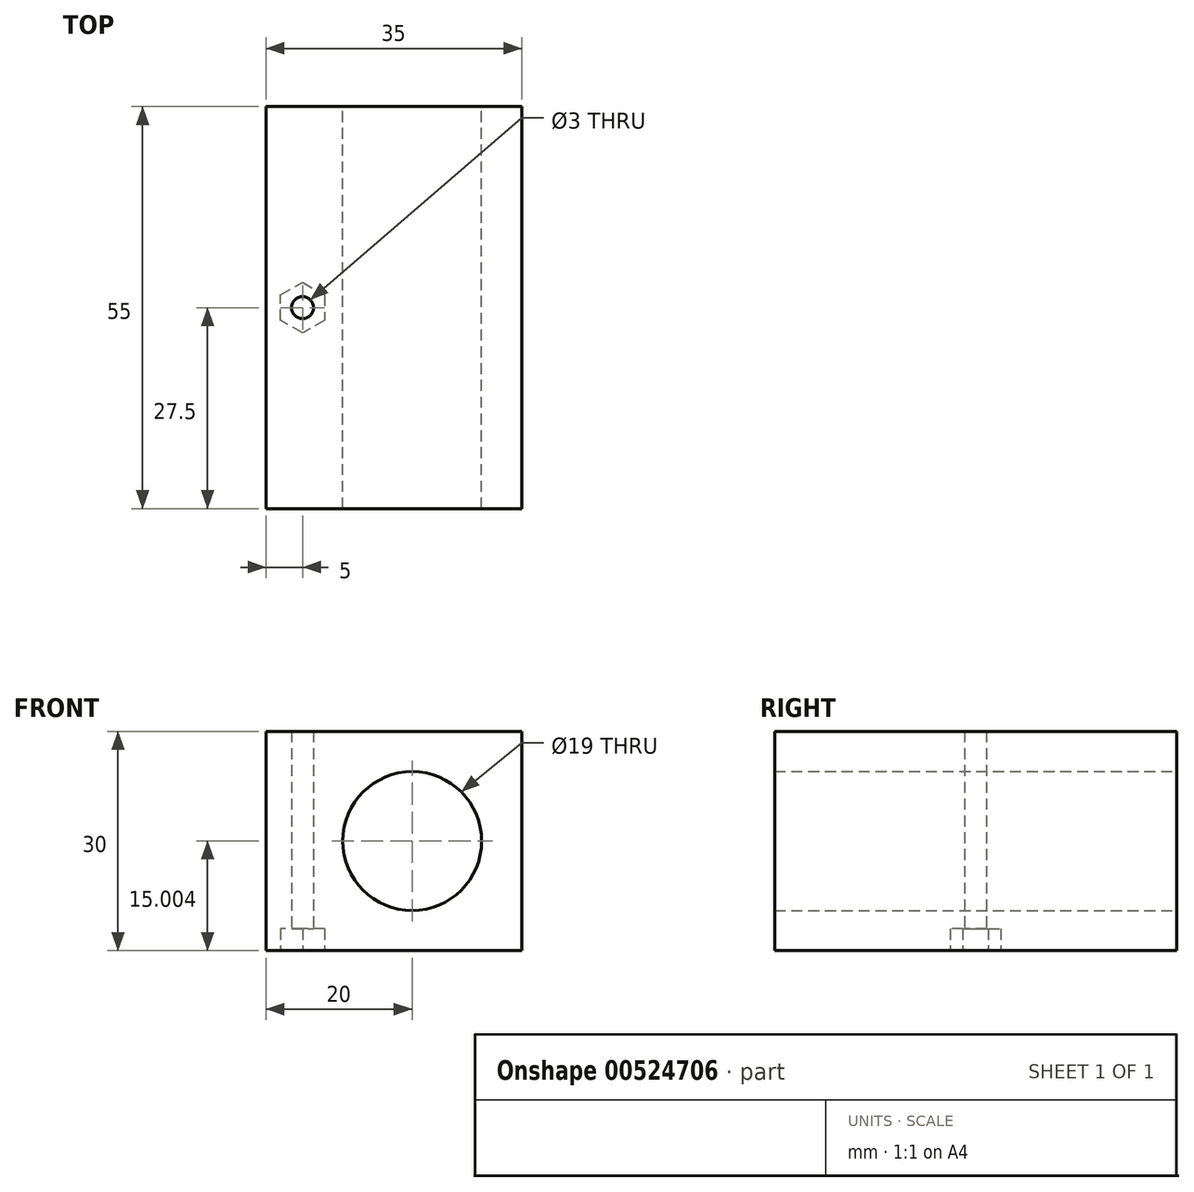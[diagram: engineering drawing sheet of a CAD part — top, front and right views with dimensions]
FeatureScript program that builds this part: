
annotation { "Feature Type Name" : "Feature", "Feature Type Description" : "" }
export const myFeature = defineFeature(function(context is Context, id is Id, definition is map)
    precondition{}
    {
        {
            var Q0;
            Q0=qCreatedBy(makeId("Front.planeOp"),FACE);
            var sketch = newSketch(context, id + "F0", { "sketchPlane" : qUnion([Q0])});
            skLineSegment(sketch, "E0.bottom", {"start": v(-25, 4.92) * mm, "end": v(10, 4.92) * mm});
            skLineSegment(sketch, "E0.top", {"start": v(-25, -25.08) * mm, "end": v(10, -25.08) * mm});
            skLineSegment(sketch, "E0.left", {"start": v(-25, 4.92) * mm, "end": v(-25, -25.08) * mm});
            skLineSegment(sketch, "E0.right", {"start": v(10, 4.92) * mm, "end": v(10, -25.08) * mm});
            skCircle(sketch, "E1", {"center": v(-5, -10.08) * mm, "radius": 9.5 * mm});
            skCircle(sketch, "E2", {"center": v(-5, -10.08) * mm, "radius": 6 * mm});
            skLineSegment(sketch, "E3.bottom", {"start": v(-25, 4.92) * mm, "end": v(0, 4.92) * mm});
            skLineSegment(sketch, "E3.top", {"start": v(-25, 27.92) * mm, "end": v(0, 27.92) * mm});
            skLineSegment(sketch, "E3.left", {"start": v(-25, 4.92) * mm, "end": v(-25, 27.92) * mm});
            skLineSegment(sketch, "E3.right", {"start": v(0, 4.92) * mm, "end": v(0, 27.92) * mm});
            skSolve(sketch);
        }
        {
            var Q0;
            Q0=makeQuery(id+"F0.imprint","IMPRINT",FACE,{"disambiguationData":[TD([[makeQuery(id+"F0.imprint","IMPRINT",EDGE,{"derivedFrom":sQuery(id+"F0.wireOp",EDGE,"E0.bottom")}),-1.0]])]});
            var Q1;
            Q1=makeQuery(id+"F0.imprint","IMPRINT",FACE,{"disambiguationData":[TD([[makeQuery(id+"F0.imprint","IMPRINT",EDGE,{"derivedFrom":sQuery(id+"F0.wireOp",EDGE,"E3.bottom")}),1.0]])]});
            extrude(context, id + "F1", {"entities" : qUnion([Q0, Q1]), "depth" : 55 * mm, "offsetDistance" : 25 * mm});
        }
        {
            var Q0;
            Q0=makeQuery(id+"F1.opExtrude","SWEPT_FACE",FACE,{"disambiguationData":[OSD([sQuery(id+"F0.wireOp",EDGE,"E0.left")])]});
            var sketch = newSketch(context, id + "F2", { "sketchPlane" : qUnion([Q0])});
            skCircle(sketch, "E4", {"center": v(12, 12.92) * mm, "radius": 4 * mm});
            skCircle(sketch, "E5", {"center": v(43, 12.92) * mm, "radius": 4 * mm});
            skSolve(sketch);
        }
        {
            var Q0;
            Q0=makeQuery(id+"F2.imprint","IMPRINT",FACE,{"disambiguationData":[TD([[makeQuery(id+"F2.imprint","IMPRINT",EDGE,{"derivedFrom":sQuery(id+"F2.wireOp",EDGE,"E4")}),1.0]])]});
            var Q1;
            Q1=makeQuery(id+"F2.imprint","IMPRINT",FACE,{"disambiguationData":[TD([[makeQuery(id+"F2.imprint","IMPRINT",EDGE,{"derivedFrom":sQuery(id+"F2.wireOp",EDGE,"E5")}),1.0]])]});
            extrude(context, id + "F3", {"entities" : qUnion([Q0, Q1]), "operationType" : NewBodyOperationType.REMOVE, "oppositeDirection" : true, "depth" : 20 * mm, "offsetDistance" : 25 * mm});
        }
        {
            var Q0;
            Q0=makeQuery(id+"F1.opExtrude","SWEPT_FACE",FACE,{"disambiguationData":[OSD([sQuery(id+"F0.wireOp",EDGE,"E0.top")])]});
            var sketch = newSketch(context, id + "F4", { "sketchPlane" : qUnion([Q0])});
            skLineSegment(sketch, "E6", {"start": v(-20, 30.96) * mm, "end": v(-23, 29.23) * mm});
            skLineSegment(sketch, "E7", {"start": v(-23, 29.23) * mm, "end": v(-23, 25.77) * mm});
            skLineSegment(sketch, "E8", {"start": v(-23, 25.77) * mm, "end": v(-20, 24.04) * mm});
            skLineSegment(sketch, "E9", {"start": v(-20, 24.04) * mm, "end": v(-17, 25.77) * mm});
            skLineSegment(sketch, "E10", {"start": v(-17, 25.77) * mm, "end": v(-17, 29.23) * mm});
            skLineSegment(sketch, "E11", {"start": v(-17, 29.23) * mm, "end": v(-20, 30.96) * mm});
            skCircle(sketch, "E12", {"center": v(-20, 27.5) * mm, "radius": 1.5 * mm});
            skSolve(sketch);
        }
        {
            var Q0;
            Q0=makeQuery(id+"F4.imprint","IMPRINT",FACE,{"disambiguationData":[TD([[makeQuery(id+"F4.imprint","IMPRINT",EDGE,{"derivedFrom":sQuery(id+"F4.wireOp",EDGE,"E6")}),1.0]])]});
            extrude(context, id + "F5", {"entities" : qUnion([Q0]), "operationType" : NewBodyOperationType.REMOVE, "oppositeDirection" : true, "depth" : 3 * mm, "offsetDistance" : 25 * mm});
        }
        {
            var Q0;
            Q0=makeQuery(id+"F5.boolean.opBoolean","SPLIT",FACE,{"disambiguationData":[TD([makeQuery(id+"F5.opExtrude","SWEPT_FACE",FACE,{"disambiguationData":[OSD([sQuery(id+"F4.wireOp",EDGE,"E12")])]})])],"derivedFrom":makeQuery(id+"F1.opExtrude","SWEPT_FACE",FACE,{"disambiguationData":[OSD([sQuery(id+"F0.wireOp",EDGE,"E0.top")])]})});
            extrude(context, id + "F6", {"entities" : qUnion([Q0]), "operationType" : NewBodyOperationType.REMOVE, "oppositeDirection" : true, "depth" : 55 * mm, "offsetDistance" : 25 * mm});
        }
    });
